# Revit family: Accessory-Tissue_Holder-KOHLER-Kumin-K-29221T
name_source: partatom
category: Specialty Equipment
units: mm (PartAtom-declared; Revit-internal decimal feet)

## family parameters
Cut with Voids When Loaded = No
Host = Face
OmniClass Number = 23.31.25.21
OmniClass Title = Toilet Paper Dispensers
Part Type = Normal
Room Calculation Point = No
Round Connector Dimension = Use Diameter
Shared = No

## types (5) — shared parameters
ADA Compliant = No
Assembly Code = C1030200
Date Modified = 08/22/2022
Default Elevation = 42"
Description = Kemei toilet paper holder (with storage platform)
Height = 2 7/8"
Length = 5 7/8"
Manufacturer = Kohler Co.
Master Format 2014 = 10 28 00
Master Format 2014 Name = Toilet, Bath, and Laundry Accessories
Material = Premium Metal Construction
Product Documentation Link = https://files.kohler.com.cn
Product Name = Kumin
Product Page URL = https://www.kohler.com.cn
URL = http://www.kohler.com.cn
WaterSense Certified = No
Width = 4 5/16"

## per-type parameters (varying)
| type | Finish | Model | Type |
| CP-Polished Chrome | Kohler-Metal-CP-Polished_Chrome | K-29221T-CP | 1 |
| BV-Brushed Bronze | Kohler-Metal-BV-Brushed_Bronze | K-29221T-BV | 2 |
| BL-Matte Black | Kohler-Metal-BL-Matte_Black | K-29221T-BL | 3 |
| 2MB-Vibrant Brushed Moderne Brass | Kohler-Metal-2MB-Vibrant_Brushed_Moderne_Brass | K-29221T-2MB | 4 |
| AF-Vibrant French Gold | Kohler-Metal-AF-Vibrant_French_Gold | K-29221T-AF | 5 |

## geometry (parser evidence)
native form markers: Sweep x6
no freeform markers — native parametric forms only
